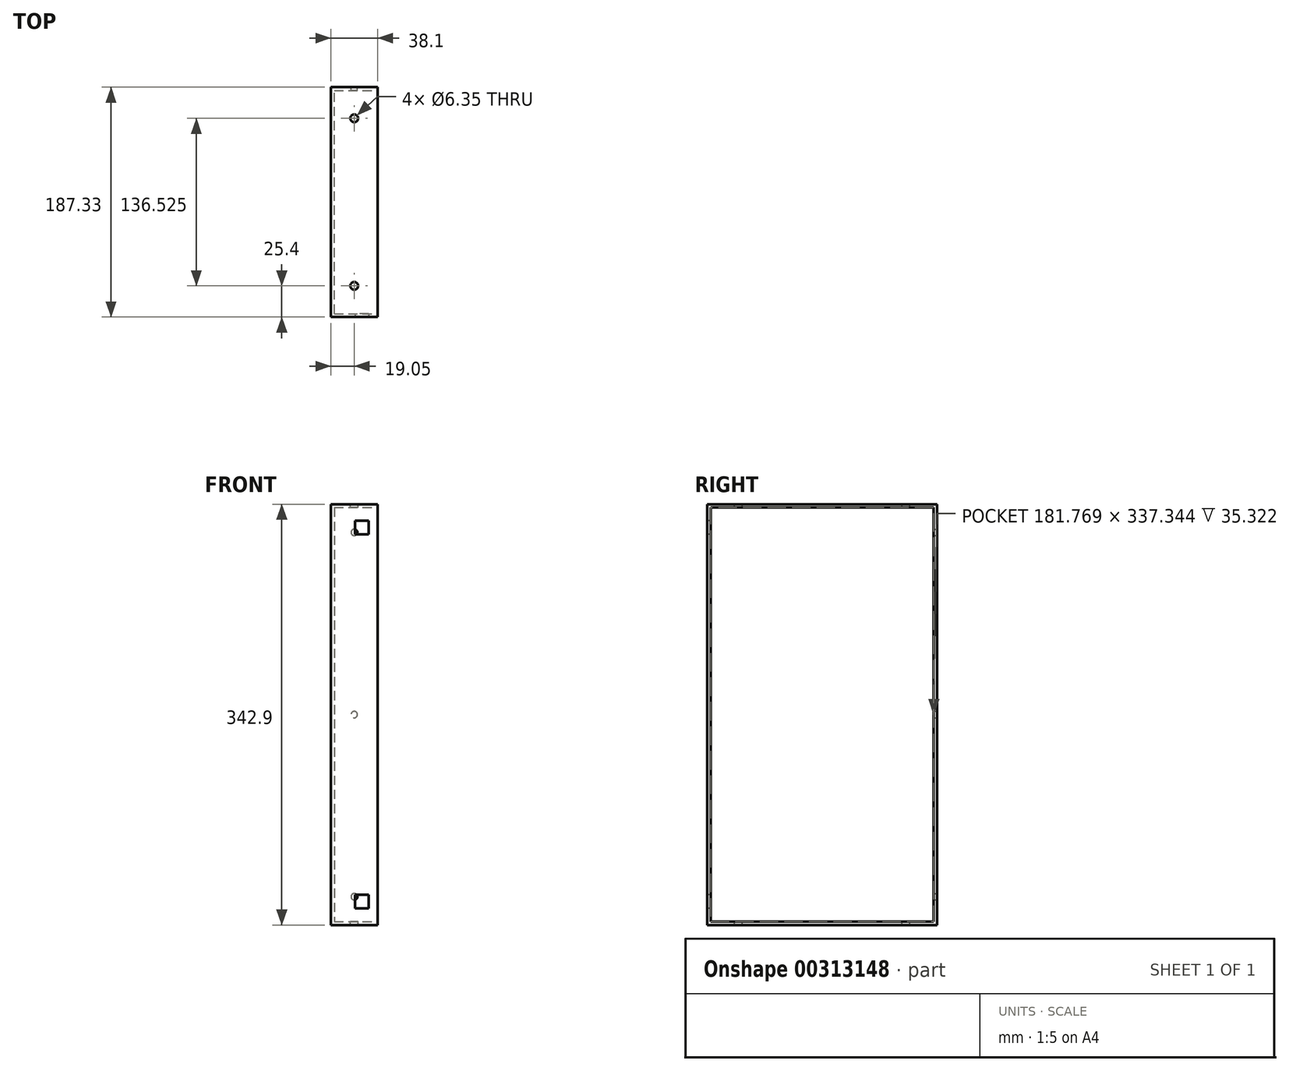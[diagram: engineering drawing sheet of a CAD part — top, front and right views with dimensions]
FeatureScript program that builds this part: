
annotation { "Feature Type Name" : "Feature", "Feature Type Description" : "" }
export const myFeature = defineFeature(function(context is Context, id is Id, definition is map)
    precondition{}
    {
        {
            var Q0;
            Q0=qCreatedBy(makeId("Top.planeOp"),FACE);
            var sketch = newSketch(context, id + "F0", { "sketchPlane" : qUnion([Q0])});
            skLineSegment(sketch, "E0.bottom", {"start": v(0, 0) * mm, "end": v(38.1, 0) * mm});
            skLineSegment(sketch, "E0.top", {"start": v(0, 187.33) * mm, "end": v(38.1, 187.33) * mm});
            skLineSegment(sketch, "E0.left", {"start": v(0, 0) * mm, "end": v(0, 187.33) * mm});
            skLineSegment(sketch, "E0.right", {"start": v(38.1, 0) * mm, "end": v(38.1, 187.33) * mm});
            skSolve(sketch);
        }
        {
            var Q0;
            Q0=qSketchRegion(id+"F0",true);
            extrude(context, id + "F1", {"entities" : qUnion([Q0]), "endBound" : BoundingType.SYMMETRIC, "depth" : 342.9 * mm});
        }
        {
            var Q0;
            Q0=makeQuery(id+"F1.opExtrude","SWEPT_FACE",FACE,{"disambiguationData":[OSD([sQuery(id+"F0.wireOp",EDGE,"E0.right")])]});
            var Q1;
            Q1=makeQuery(id+"F1.opExtrude","SWEPT_FACE",FACE,{"disambiguationData":[OSD([sQuery(id+"F0.wireOp",EDGE,"06e66f88-2ae3-45e9-895b-eb5daa671fde.1.0.3")])]});
            shell(context, id + "F2", {"entities" : qUnion([Q0, Q1]), "thickness" : 2.78 * mm});
        }
        {
            var Q0;
            Q0=makeQuery(id+"F1.opExtrude","SWEPT_FACE",FACE,{"disambiguationData":[OSD([sQuery(id+"F0.wireOp",EDGE,"E0.top")])]});
            var sketch = newSketch(context, id + "F3", { "sketchPlane" : qUnion([Q0])});
            skCircle(sketch, "E1", {"center": v(-19.05, 148.43) * mm, "radius": 2.58 * mm});
            skPoint(sketch, "E1.centerSnap0", {"position": v(-19.05, 171.45) * mm});
            skCircle(sketch, "E2", {"center": v(-19.05, 0) * mm, "radius": 2.58 * mm});
            skCircle(sketch, "E3", {"center": v(-19.05, -148.43) * mm, "radius": 2.58 * mm});
            skLineSegment(sketch, "E4", {"start": v(-19.05, 148.43) * mm, "end": v(-19.05, -148.43) * mm, "construction": true});
            skSolve(sketch);
        }
        {
            var Q0;
            Q0=qSketchRegion(id+"F3",true);
            extrude(context, id + "F4", {"entities" : qUnion([Q0]), "operationType" : NewBodyOperationType.REMOVE, "endBound" : BoundingType.UP_TO_NEXT, "oppositeDirection" : true, "depth" : 25.4 * mm});
        }
        {
            var Q0;
            Q0=makeQuery(id+"F1.opExtrude","CAP_FACE",FACE,{"disambiguationData":[OSD([sQuery(id+"F0.wireOp",EDGE,"E0.bottom"),sQuery(id+"F0.wireOp",EDGE,"E0.top"),sQuery(id+"F0.wireOp",EDGE,"E0.left"),sQuery(id+"F0.wireOp",EDGE,"E0.right")])],"isStart":false});
            var sketch = newSketch(context, id + "F5", { "sketchPlane" : qUnion([Q0])});
            skCircle(sketch, "E5", {"center": v(19.05, 161.92) * mm, "radius": 3.17 * mm});
            skPoint(sketch, "E5.centerSnap0", {"position": v(19.05, 187.33) * mm});
            skCircle(sketch, "E6", {"center": v(19.05, 25.4) * mm, "radius": 3.17 * mm});
            skLineSegment(sketch, "E7", {"start": v(19.05, 161.92) * mm, "end": v(19.05, 25.4) * mm, "construction": true});
            skPoint(sketch, "E8", {"position": v(19.05, 93.66) * mm});
            skSolve(sketch);
        }
        {
            var Q0;
            Q0=qSketchRegion(id+"F5",true);
            extrude(context, id + "F6", {"entities" : qUnion([Q0]), "operationType" : NewBodyOperationType.REMOVE, "endBound" : BoundingType.THROUGH_ALL, "oppositeDirection" : true, "depth" : 25.4 * mm});
        }
        {
            var Q0;
            Q0=makeQuery(id+"F1.opExtrude","SWEPT_FACE",FACE,{"disambiguationData":[OSD([sQuery(id+"F0.wireOp",EDGE,"E0.bottom")])]});
            var sketch = newSketch(context, id + "F7", { "sketchPlane" : qUnion([Q0])});
            skLineSegment(sketch, "E9.bottom", {"start": v(30.96, 146.84) * mm, "end": v(19.84, 146.84) * mm});
            skLineSegment(sketch, "E9.top", {"start": v(30.96, 157.96) * mm, "end": v(19.84, 157.96) * mm});
            skLineSegment(sketch, "E9.left", {"start": v(30.96, 146.84) * mm, "end": v(30.96, 157.96) * mm});
            skLineSegment(sketch, "E9.right", {"start": v(19.84, 146.84) * mm, "end": v(19.84, 157.96) * mm});
            skPoint(sketch, "E9.middle", {"position": v(25.4, 152.4) * mm});
            skLineSegment(sketch, "E10.bottom", {"start": v(30.96, -146.84) * mm, "end": v(19.84, -146.84) * mm});
            skLineSegment(sketch, "E10.top", {"start": v(30.96, -157.96) * mm, "end": v(19.84, -157.96) * mm});
            skLineSegment(sketch, "E10.left", {"start": v(30.96, -146.84) * mm, "end": v(30.96, -157.96) * mm});
            skLineSegment(sketch, "E10.right", {"start": v(19.84, -146.84) * mm, "end": v(19.84, -157.96) * mm});
            skPoint(sketch, "E10.middle", {"position": v(25.4, -152.4) * mm});
            skSolve(sketch);
        }
        {
            var Q0;
            Q0 = qSketchRegion(id + "F7", true);
            extrude(context, id + "F8", {"entities" : qUnion([Q0]), "operationType" : NewBodyOperationType.REMOVE, "endBound" : BoundingType.UP_TO_NEXT, "oppositeDirection" : true, "depth" : 25.4 * mm});
        }
    });
